# Revit family: Gira_235900
name_source: partatom
category: Electrical Fixtures
revit_build: Autodesk Revit 2017 (Build: 20160225_1515(x64)
units: mm (PartAtom-declared; Revit-internal decimal feet)

## family parameters
Cut with Voids When Loaded = No
Host = Face
Maintain Annotation Orientation = Yes
Part Type = Normal
Room Calculation Point = No
Round Connector Dimension = Use Diameter
Shared = No

## types (1)
- USB-Spannungsversorgung 2f Typ A/A Einsatz
    Anzahl der Ausgänge = 2
    Ausführung = Buchse
    Ausgangsspannung = 5 Volt
    Available = Yes
    Betriebsspannung = 110 - 240
    Category = USB-Spannungsversorgung
    Data sheet (1) = https://katalog.gira.de
    Default Elevation = 1219 mm
    Farbe = sonstige
    Frequenz = 50 - 60
    GTIN = 4010337084655
    HAN = 235900
    HeinzeBIM = https://bimportal.heinze.de
    Keynote = Einsatz_1fach
    Manufacturer URL = https://www.gira.de
    Max. Ausgangsstrom = 1,4 Ampere
    Montageart = unter Putz
    Name = USB-Spannungsversorgung 2f Typ A/A Einsatz
    Region = DE
    URL = http://katalog.gira.de

## geometry (parser evidence)
native form markers: Blend x2, Sweep x3
no freeform markers — native parametric forms only
